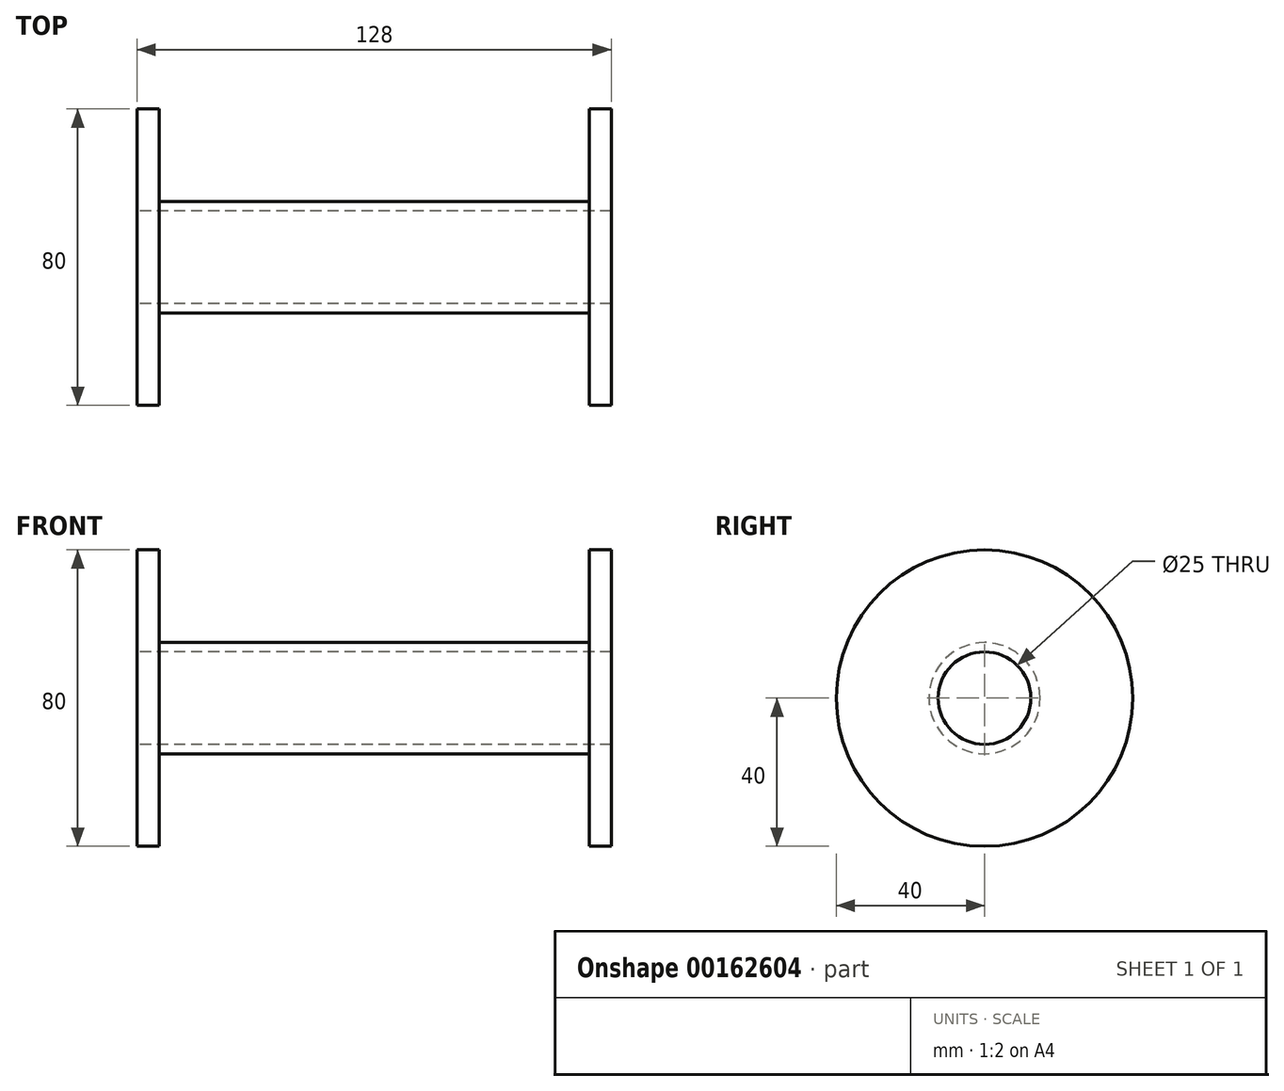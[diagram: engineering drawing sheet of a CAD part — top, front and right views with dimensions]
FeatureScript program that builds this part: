
annotation { "Feature Type Name" : "Feature", "Feature Type Description" : "" }
export const myFeature = defineFeature(function(context is Context, id is Id, definition is map)
    precondition{}
    {
        {
            var Q0;
            Q0=qCreatedBy(makeId("Front.planeOp"),FACE);
            var sketch = newSketch(context, id + "F0", { "sketchPlane" : qUnion([Q0])});
            skLineSegment(sketch, "E0", {"start": v(0, 0) * mm, "end": v(128, 0) * mm, "construction": true});
            skLineSegment(sketch, "E1", {"start": v(0, 12.5) * mm, "end": v(128, 12.5) * mm});
            skLineSegment(sketch, "E2", {"start": v(0, 12.5) * mm, "end": v(0, 40) * mm});
            skLineSegment(sketch, "E3", {"start": v(0, 40) * mm, "end": v(6, 40) * mm});
            skLineSegment(sketch, "E4", {"start": v(6, 40) * mm, "end": v(6, 15) * mm});
            skLineSegment(sketch, "E5", {"start": v(6, 15) * mm, "end": v(122, 15) * mm});
            skLineSegment(sketch, "E6", {"start": v(122, 15) * mm, "end": v(122, 40) * mm});
            skLineSegment(sketch, "E7", {"start": v(122, 40) * mm, "end": v(128, 40) * mm});
            skLineSegment(sketch, "E8", {"start": v(128, 40) * mm, "end": v(128, 12.5) * mm});
            skSolve(sketch);
        }
        {
            var Q0;
            Q0=qSketchRegion(id+"F0",true);
            var Q1;
            Q1=sQuery(id+"F0.wireOp",EDGE,"E0");
            revolve(context, id + "F1", {"entities" : qUnion([Q0]), "axis" : qUnion([Q1]), "revolveType" : RevolveType.FULL});
        }
    });
